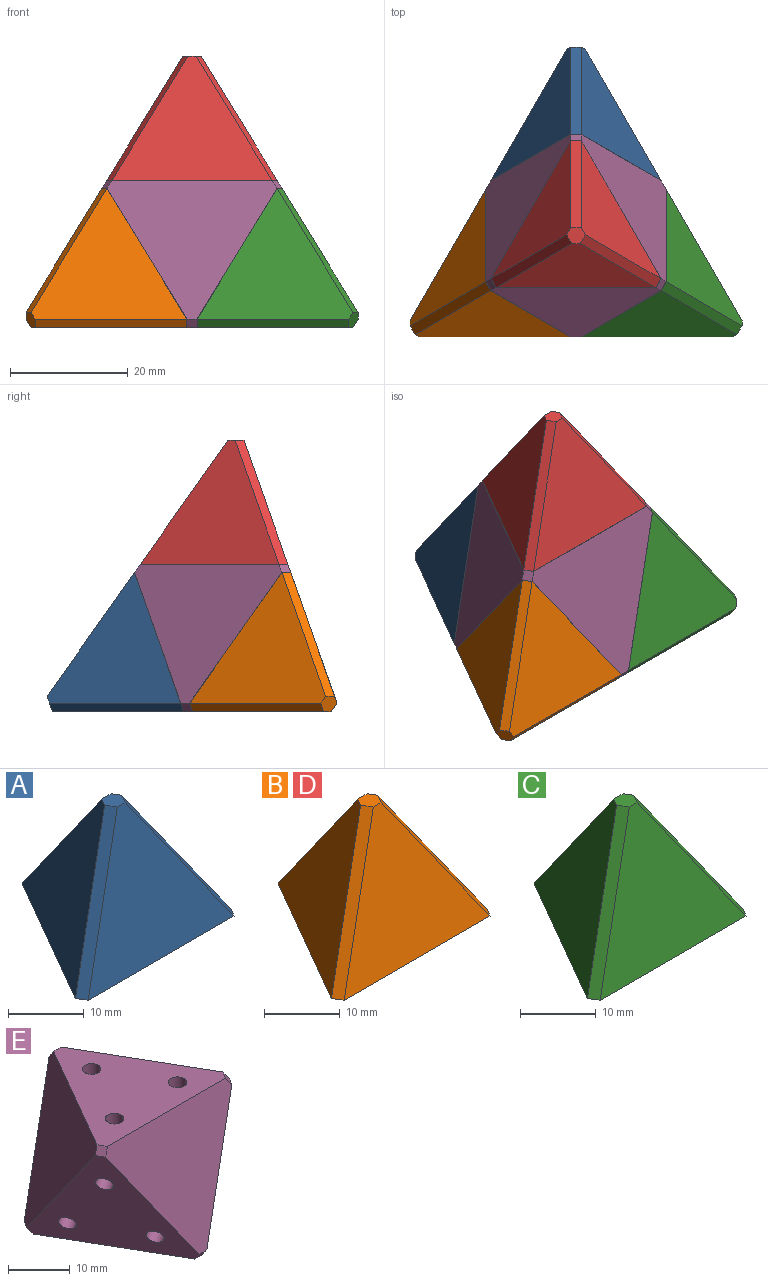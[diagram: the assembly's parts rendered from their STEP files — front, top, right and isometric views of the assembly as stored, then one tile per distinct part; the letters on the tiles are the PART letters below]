
ASSEMBLY  parts=5 mates=4
PART A: 14 faces, bbox 28.9x25x21 mm
  f0: plane 3.18x2.75mm, normal (0,0,1), area 6.5mm2, adj f2,f3,f4,f5,f6,f7
  f1: plane 28.89x25.02mm, normal (0,0,-1), area 380.8mm2, adj f2,f3,f4,f5,f6,f7,f8,f10
  f2: plane 23.52x21mm, normal (-0.82,0.47,0.33), area 318.5mm2, adj f0,f1,f5,f6
  f3: plane 23.52x21mm, normal (0.82,0.47,0.33), area 318.5mm2, adj f0,f1,f6,f7
  f4: plane 27.15x21mm, normal (0,-0.94,0.33), area 318.5mm2, adj f0,f1,f5,f7
  f5: plane 21x13.72mm, normal (-0.71,-0.41,0.58), area 44.5mm2, adj f0,f1,f2,f4
  f6: plane 21x14.84mm, normal (0,0.82,0.58), area 44.5mm2, adj f0,f1,f2,f3
  f7: plane 21x13.72mm, normal (0.71,-0.41,0.58), area 44.5mm2, adj f0,f1,f3,f4
  f8: cylinder r=1.5mm len=5mm, axis (0,0,-1), area 47.1mm2, adj f1,f9
  f9: plane 3x3mm, normal (0,0,-1), area 7.1mm2, adj f8
  f10: cylinder r=1.5mm len=5mm, axis (0,0,-1), area 47.1mm2, adj f1,f11
  f11: plane 3x3mm, normal (0,0,-1), area 7.1mm2, adj f10
  f12: cylinder r=1.5mm len=5mm, axis (0,0,-1), area 47.1mm2, adj f1,f13
  f13: plane 3x3mm, normal (0,0,-1), area 7.1mm2, adj f12
PART B: 14 faces, bbox 28.9x25x21 mm
  f0: plane 3.18x2.75mm, normal (0,0,1), area 6.5mm2, adj f2,f3,f4,f5,f6,f7
  f1: plane 28.89x25.02mm, normal (0,0,-1), area 380.8mm2, adj f2,f3,f4,f5,f6,f7,f8,f10
  f2: plane 23.52x21mm, normal (-0.82,0.47,0.33), area 318.5mm2, adj f0,f1,f5,f6
  f3: plane 23.52x21mm, normal (0.82,0.47,0.33), area 318.5mm2, adj f0,f1,f6,f7
  f4: plane 27.15x21mm, normal (0,-0.94,0.33), area 318.5mm2, adj f0,f1,f5,f7
  f5: plane 21x13.72mm, normal (-0.71,-0.41,0.58), area 44.5mm2, adj f0,f1,f2,f4
  f6: plane 21x14.84mm, normal (0,0.82,0.58), area 44.5mm2, adj f0,f1,f2,f3
  f7: plane 21x13.72mm, normal (0.71,-0.41,0.58), area 44.5mm2, adj f0,f1,f3,f4
  f8: cylinder r=1.5mm len=5mm, axis (0,0,-1), area 47.1mm2, adj f1,f9
  f9: plane 3x3mm, normal (0,0,-1), area 7.1mm2, adj f8
  f10: cylinder r=1.5mm len=5mm, axis (0,0,-1), area 47.1mm2, adj f1,f11
  f11: plane 3x3mm, normal (0,0,-1), area 7.1mm2, adj f10
  f12: cylinder r=1.5mm len=5mm, axis (0,0,-1), area 47.1mm2, adj f1,f13
  f13: plane 3x3mm, normal (0,0,-1), area 7.1mm2, adj f12
PART C: 14 faces, bbox 28.9x25x21 mm
  f0: plane 3.18x2.75mm, normal (0,0,1), area 6.5mm2, adj f2,f3,f4,f5,f6,f7
  f1: plane 28.89x25.02mm, normal (0,0,-1), area 380.8mm2, adj f2,f3,f4,f5,f6,f7,f8,f10
  f2: plane 23.52x21mm, normal (-0.82,0.47,0.33), area 318.5mm2, adj f0,f1,f5,f6
  f3: plane 23.52x21mm, normal (0.82,0.47,0.33), area 318.5mm2, adj f0,f1,f6,f7
  f4: plane 27.15x21mm, normal (0,-0.94,0.33), area 318.5mm2, adj f0,f1,f5,f7
  f5: plane 21x13.72mm, normal (-0.71,-0.41,0.58), area 44.5mm2, adj f0,f1,f2,f4
  f6: plane 21x14.84mm, normal (0,0.82,0.58), area 44.5mm2, adj f0,f1,f2,f3
  f7: plane 21x13.72mm, normal (0.71,-0.41,0.58), area 44.5mm2, adj f0,f1,f3,f4
  f8: cylinder r=1.5mm len=5mm, axis (0,0,-1), area 47.1mm2, adj f1,f9
  f9: plane 3x3mm, normal (0,0,-1), area 7.1mm2, adj f8
  f10: cylinder r=1.5mm len=5mm, axis (0,0,-1), area 47.1mm2, adj f1,f11
  f11: plane 3x3mm, normal (0,0,-1), area 7.1mm2, adj f10
  f12: cylinder r=1.5mm len=5mm, axis (0,0,-1), area 47.1mm2, adj f1,f13
  f13: plane 3x3mm, normal (0,0,-1), area 7.1mm2, adj f12
PART D: same geometry as B
PART E: 38 faces, bbox 30.6x34.4x26.4 mm
  f0: plane 28.87x25.03mm, normal (0,0,-1), area 402mm2, adj f5,f6,f7,f32,f33,f35
  f1: plane 24.98x23.58mm, normal (-0.82,0.47,0.33), area 402mm2, adj f4,f5,f6,f35,f36,f37
  f2: plane 28.87x23.6mm, normal (0,-0.94,0.33), area 402mm2, adj f4,f6,f7,f32,f34,f36
  f3: plane 24.98x23.58mm, normal (0.82,0.47,0.33), area 402mm2, adj f4,f5,f7,f33,f34,f37
  f4: plane 28.87x25.03mm, normal (0,0,1), area 380.9mm2, adj f1,f2,f3,f8,f10,f12,f34,f36
  f5: plane 28.87x23.59mm, normal (0,0.94,-0.33), area 380.8mm2, adj f0,f1,f3,f14,f16,f18,f33,f35
  f6: plane 24.98x23.57mm, normal (-0.82,-0.47,-0.33), area 380.8mm2, adj f0,f1,f2,f20,f22,f24,f32,f35
  f7: plane 24.98x23.57mm, normal (0.82,-0.47,-0.33), area 380.8mm2, adj f0,f2,f3,f26,f28,f30,f32,f33
  f8: cylinder r=1.5mm len=5mm, axis (0,0,-1), area 47.1mm2, adj f4,f9
  f9: plane 3x3mm, normal (0,0,1), area 7.1mm2, adj f8
  f10: cylinder r=1.5mm len=5mm, axis (0,0,-1), area 47.1mm2, adj f4,f11
  f11: plane 3x3mm, normal (0,0,1), area 7.1mm2, adj f10
  f12: cylinder r=1.5mm len=5mm, axis (0,0,-1), area 47.1mm2, adj f4,f13
  f13: plane 3x3mm, normal (0,0,1), area 7.1mm2, adj f12
  f14: cylinder r=1.5mm len=5.71mm, axis (0,-0.94,0.33), area 47.1mm2, adj f5,f15
  f15: plane 3x2.83mm, normal (0,0.94,-0.33), area 7.1mm2, adj f14
  f16: cylinder r=1.5mm len=5.71mm, axis (0,-0.94,0.33), area 47.1mm2, adj f5,f17
  f17: plane 3x2.83mm, normal (0,0.94,-0.33), area 7.1mm2, adj f16
  f18: cylinder r=1.5mm len=5.71mm, axis (0,-0.94,0.33), area 47.1mm2, adj f5,f19
  f19: plane 3x2.83mm, normal (0,0.94,-0.33), area 7.1mm2, adj f18
  f20: cylinder r=1.5mm len=5.81mm, axis (0.82,0.47,0.33), area 47.1mm2, adj f6,f21
  f21: plane 2.83x2.65mm, normal (-0.82,-0.47,-0.33), area 7.1mm2, adj f20
  f22: cylinder r=1.5mm len=5.81mm, axis (0.82,0.47,0.33), area 47.1mm2, adj f6,f23
  f23: plane 2.83x2.65mm, normal (-0.82,-0.47,-0.33), area 7.1mm2, adj f22
  f24: cylinder r=1.5mm len=5.81mm, axis (0.82,0.47,0.33), area 47.1mm2, adj f6,f25
  f25: plane 2.83x2.65mm, normal (-0.82,-0.47,-0.33), area 7.1mm2, adj f24
  f26: cylinder r=1.5mm len=5.81mm, axis (-0.82,0.47,0.33), area 47.1mm2, adj f7,f27
  f27: plane 2.83x2.65mm, normal (0.82,-0.47,-0.33), area 7.1mm2, adj f26
  f28: cylinder r=1.5mm len=5.81mm, axis (-0.82,0.47,0.33), area 47.1mm2, adj f7,f29
  f29: plane 2.83x2.65mm, normal (0.82,-0.47,-0.33), area 7.1mm2, adj f28
  f30: cylinder r=1.5mm len=5.81mm, axis (-0.82,0.47,0.33), area 47.1mm2, adj f7,f31
  f31: plane 2.83x2.65mm, normal (0.82,-0.47,-0.33), area 7.1mm2, adj f30
  f32: sphere r=20.44mm, area 3.1mm2, adj f0,f2,f6,f7
  f33: sphere r=20.44mm, area 3mm2, adj f0,f3,f5,f7
  f34: sphere r=20.44mm, area 3.1mm2, adj f2,f3,f4,f7
  f35: sphere r=20.44mm, area 3.1mm2, adj f0,f1,f5,f6
  f36: sphere r=20.44mm, area 3.1mm2, adj f1,f2,f4,f6
  f37: sphere r=20.44mm, area 3.1mm2, adj f1,f3,f4,f5
PLACE A rot(axis=(0,-0.82,-0.58),180deg) t=(35,-11.78,16.67)mm
PLACE B rot(axis=(-0.71,-0.41,0.58),180deg) t=(10.2,5.89,16.67)mm
PLACE C rot(axis=(-0.71,0.41,-0.58),180deg) t=(-10.2,-14.32,45.24)mm
PLACE D at identity
PLACE E at identity fixed
MATE fastened E.f6 <-> B.f1  axis (-0.82,-0.47,-0.33) through (-10.21,-5.89,8.33)mm
MATE fastened E.f5 <-> A.f1  axis (0,0.94,-0.33) through (0,11.79,8.33)mm
MATE fastened E.f4 <-> D.f1  axis (0,0,1) through (0,0,25)mm
MATE fastened E.f7 <-> C.f1  axis (0.82,-0.47,-0.33) through (10.21,-5.89,8.33)mm
